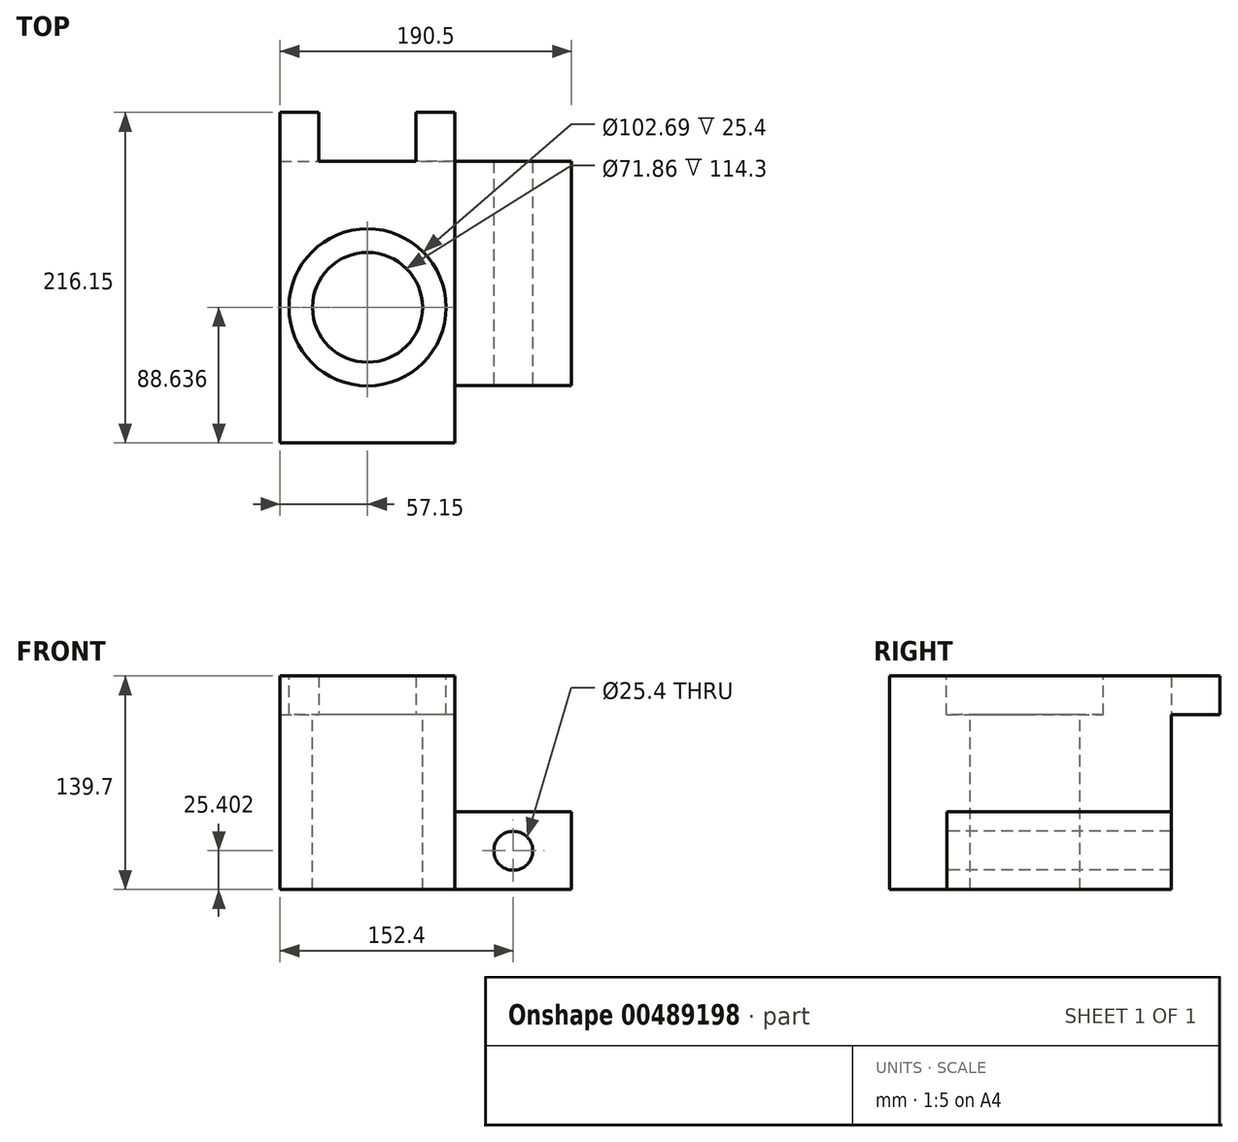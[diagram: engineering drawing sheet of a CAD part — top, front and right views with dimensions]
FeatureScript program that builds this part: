
annotation { "Feature Type Name" : "Feature", "Feature Type Description" : "" }
export const myFeature = defineFeature(function(context is Context, id is Id, definition is map)
    precondition{}
    {
        {
            var Q0;
            Q0=qCreatedBy(makeId("Front.planeOp"),FACE);
            var sketch = newSketch(context, id + "F0", { "sketchPlane" : qUnion([Q0])});
            skLineSegment(sketch, "E0.bottom", {"start": v(-114.3, 52.28) * mm, "end": v(0, 52.28) * mm});
            skLineSegment(sketch, "E0.top", {"start": v(-114.3, -87.42) * mm, "end": v(0, -87.42) * mm});
            skLineSegment(sketch, "E0.left", {"start": v(-114.3, 52.28) * mm, "end": v(-114.3, -87.42) * mm});
            skLineSegment(sketch, "E0.right", {"start": v(0, 52.28) * mm, "end": v(0, -87.42) * mm});
            skLineSegment(sketch, "E1.bottom", {"start": v(76.2, -36.62) * mm, "end": v(0, -36.62) * mm});
            skLineSegment(sketch, "E1.top", {"start": v(76.2, -87.42) * mm, "end": v(0, -87.42) * mm});
            skLineSegment(sketch, "E1.left", {"start": v(76.2, -36.62) * mm, "end": v(76.2, -87.42) * mm});
            skLineSegment(sketch, "E1.right", {"start": v(0, -36.62) * mm, "end": v(0, -87.42) * mm});
            skCircle(sketch, "E2", {"center": v(38.1, -62.02) * mm, "radius": 12.7 * mm});
            skPoint(sketch, "E2.centerSnap0", {"position": v(0, -62.02) * mm});
            skSolve(sketch);
        }
        {
            var Q0;
            Q0=makeQuery(id+"F0.imprint","IMPRINT",FACE,{"disambiguationData":[TD([[makeQuery(id+"F0.imprint","IMPRINT",EDGE,{"derivedFrom":sQuery(id+"F0.wireOp",EDGE,"E0.bottom")}),-1.0]])]});
            var Q1;
            Q1=makeQuery(id+"F0.imprint","IMPRINT",FACE,{"disambiguationData":[TD([[makeQuery(id+"F0.imprint","IMPRINT",EDGE,{"derivedFrom":sQuery(id+"F0.wireOp",EDGE,"E1.bottom")}),1.0]])]});
            extrude(context, id + "F1", {"entities" : qUnion([Q0, Q1]), "oppositeDirection" : true, "depth" : 184.15 * mm});
        }
        {
            var Q0;
            Q0=makeQuery(id+"F1.opExtrude","SWEPT_FACE",FACE,{"disambiguationData":[OSD([sQuery(id+"F0.wireOp",EDGE,"E0.bottom")])]});
            var sketch = newSketch(context, id + "F2", { "sketchPlane" : qUnion([Q0])});
            skCircle(sketch, "E3", {"center": v(-57.15, 88.64) * mm, "radius": 51.34 * mm});
            skCircle(sketch, "E4", {"center": v(-57.15, 88.64) * mm, "radius": 35.93 * mm});
            skSolve(sketch);
        }
        {
            var Q0;
            Q0=makeQuery(id+"F2.imprint","IMPRINT",FACE,{"disambiguationData":[TD([[makeQuery(id+"F2.imprint","IMPRINT",EDGE,{"derivedFrom":sQuery(id+"F2.wireOp",EDGE,"E3")}),1.0]])]});
            extrude(context, id + "F3", {"entities" : qUnion([Q0]), "operationType" : NewBodyOperationType.REMOVE, "oppositeDirection" : true, "depth" : 25.4 * mm});
        }
        {
            var Q0;
            Q0=makeQuery(id+"F3.boolean.opBoolean","SPLIT",FACE,{"disambiguationData":[TD([makeQuery(id+"F3.opExtrude","SWEPT_FACE",FACE,{"disambiguationData":[OSD([sQuery(id+"F2.wireOp",EDGE,"E4")])]})])],"derivedFrom":makeQuery(id+"F1.opExtrude","SWEPT_FACE",FACE,{"disambiguationData":[OSD([sQuery(id+"F0.wireOp",EDGE,"E0.bottom")])]})});
            extrude(context, id + "F4", {"entities" : qUnion([Q0]), "operationType" : NewBodyOperationType.REMOVE, "oppositeDirection" : true, "depth" : 311.15 * mm});
        }
        {
            var Q0;
            Q0=makeQuery(id+"F1.opExtrude","CAP_FACE",FACE,{"disambiguationData":[OSD([sQuery(id+"F0.wireOp",EDGE,"E0.bottom"),sQuery(id+"F0.wireOp",EDGE,"E0.top"),sQuery(id+"F0.wireOp",EDGE,"E0.left"),sQuery(id+"F0.wireOp",EDGE,"E0.right"),sQuery(id+"F0.wireOp",EDGE,"E1.bottom"),sQuery(id+"F0.wireOp",EDGE,"E1.top"),sQuery(id+"F0.wireOp",EDGE,"E1.left"),sQuery(id+"F0.wireOp",EDGE,"E2")])],"isStart":false});
            var sketch = newSketch(context, id + "F5", { "sketchPlane" : qUnion([Q0])});
            skLineSegment(sketch, "E5.bottom", {"start": v(0, 52.28) * mm, "end": v(25.4, 52.28) * mm});
            skLineSegment(sketch, "E5.top", {"start": v(0, 26.88) * mm, "end": v(25.4, 26.88) * mm});
            skLineSegment(sketch, "E5.left", {"start": v(0, 52.28) * mm, "end": v(0, 26.88) * mm});
            skLineSegment(sketch, "E5.right", {"start": v(25.4, 52.28) * mm, "end": v(25.4, 26.88) * mm});
            skLineSegment(sketch, "E6.bottom", {"start": v(114.3, 52.28) * mm, "end": v(88.9, 52.28) * mm});
            skLineSegment(sketch, "E6.top", {"start": v(114.3, 26.88) * mm, "end": v(88.9, 26.88) * mm});
            skLineSegment(sketch, "E6.left", {"start": v(114.3, 52.28) * mm, "end": v(114.3, 26.88) * mm});
            skLineSegment(sketch, "E6.right", {"start": v(88.9, 52.28) * mm, "end": v(88.9, 26.88) * mm});
            skSolve(sketch);
        }
        {
            var Q0;
            Q0=makeQuery(id+"F5.imprint","IMPRINT",FACE,{"disambiguationData":[TD([[makeQuery(id+"F5.imprint","IMPRINT",EDGE,{"derivedFrom":sQuery(id+"F5.wireOp",EDGE,"E5.bottom")}),1.0]])]});
            var Q1;
            Q1=makeQuery(id+"F5.imprint","IMPRINT",FACE,{"disambiguationData":[TD([[makeQuery(id+"F5.imprint","IMPRINT",EDGE,{"derivedFrom":sQuery(id+"F5.wireOp",EDGE,"E6.bottom")}),1.0]])]});
            extrude(context, id + "F6", {"entities" : qUnion([Q0, Q1]), "operationType" : NewBodyOperationType.ADD, "depth" : 32 * mm});
        }
        {
            var Q0;
            Q0=makeQuery(id+"F1.opExtrude","CAP_FACE",FACE,{"disambiguationData":[OSD([sQuery(id+"F0.wireOp",EDGE,"E0.bottom"),sQuery(id+"F0.wireOp",EDGE,"E0.top"),sQuery(id+"F0.wireOp",EDGE,"E0.left"),sQuery(id+"F0.wireOp",EDGE,"E0.right"),sQuery(id+"F0.wireOp",EDGE,"E1.bottom"),sQuery(id+"F0.wireOp",EDGE,"E1.top"),sQuery(id+"F0.wireOp",EDGE,"E1.left"),sQuery(id+"F0.wireOp",EDGE,"E2")])],"isStart":true});
            var sketch = newSketch(context, id + "F7", { "sketchPlane" : qUnion([Q0])});
            skLineSegment(sketch, "E7.bottom", {"start": v(0, -36.62) * mm, "end": v(76.2, -36.62) * mm});
            skLineSegment(sketch, "E7.top", {"start": v(0, -87.42) * mm, "end": v(76.2, -87.42) * mm});
            skLineSegment(sketch, "E7.left", {"start": v(0, -36.62) * mm, "end": v(0, -87.42) * mm});
            skLineSegment(sketch, "E7.right", {"start": v(76.2, -36.62) * mm, "end": v(76.2, -87.42) * mm});
            skSolve(sketch);
        }
        {
            var Q0;
            Q0=makeQuery(id+"F7.imprint","IMPRINT",FACE,{"disambiguationData":[TD([[makeQuery(id+"F7.imprint","IMPRINT",EDGE,{"derivedFrom":sQuery(id+"F7.wireOp",EDGE,"E7.bottom")}),1.0]])]});
            extrude(context, id + "F8", {"entities" : qUnion([Q0]), "operationType" : NewBodyOperationType.REMOVE, "oppositeDirection" : true, "depth" : 37.6 * mm});
        }
        {
            var Q0;
            Q0=makeQuery(id+"F6.boolean.opBoolean","MERGE",FACE,{"derivedFrom":[makeQuery(id+"F1.opExtrude","SWEPT_FACE",FACE,{"disambiguationData":[OSD([sQuery(id+"F0.wireOp",EDGE,"E0.left")])]}),makeQuery(id+"F6.opExtrude","SWEPT_FACE",FACE,{"disambiguationData":[OSD([sQuery(id+"F5.wireOp",EDGE,"E6.left")])]})]});
            extrude(context, id + "F9", {"entities" : qUnion([Q0]), "operationType" : NewBodyOperationType.ADD, "oppositeDirection" : true, "depth" : 0.76 * mm});
        }
    });
